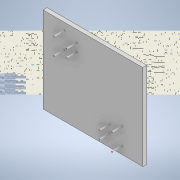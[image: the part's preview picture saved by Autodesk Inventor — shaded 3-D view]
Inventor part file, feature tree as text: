
AUTODESK INVENTOR PART (.ipt)
format: ipt  version: 2022 (Build 260153000, 153)  size: 129,536 bytes
history: native  units: mm
features: extrude x3, sketch x2, other x1
ambient origin geometry x8: Origin, YZ Plane, XZ Plane, XY Plane, X Axis, Y Axis, Z Axis, Center Point
bodies: Body1 (feature_tree)
feature tree (6):
  other  "Sólido1"
  extrude  "Extrusión1"  Depth=430.0mm
  sketch  "Boceto7"  dims[d2=20.0mm d3=0.0mm d22=20.0mm d23=6.0mm d24=6.0mm d25=50.0mm d26=30.0mm d27=50.0mm d28=0.0mm d29=50.0mm d30=0.0mm]
  extrude  "Extrusión7"  Depth=20.0mm
  extrude  "Extrusión8"  Depth=50.0mm
  sketch  "Boceto1"  dims[d0=500.0mm d1=430.0mm]
